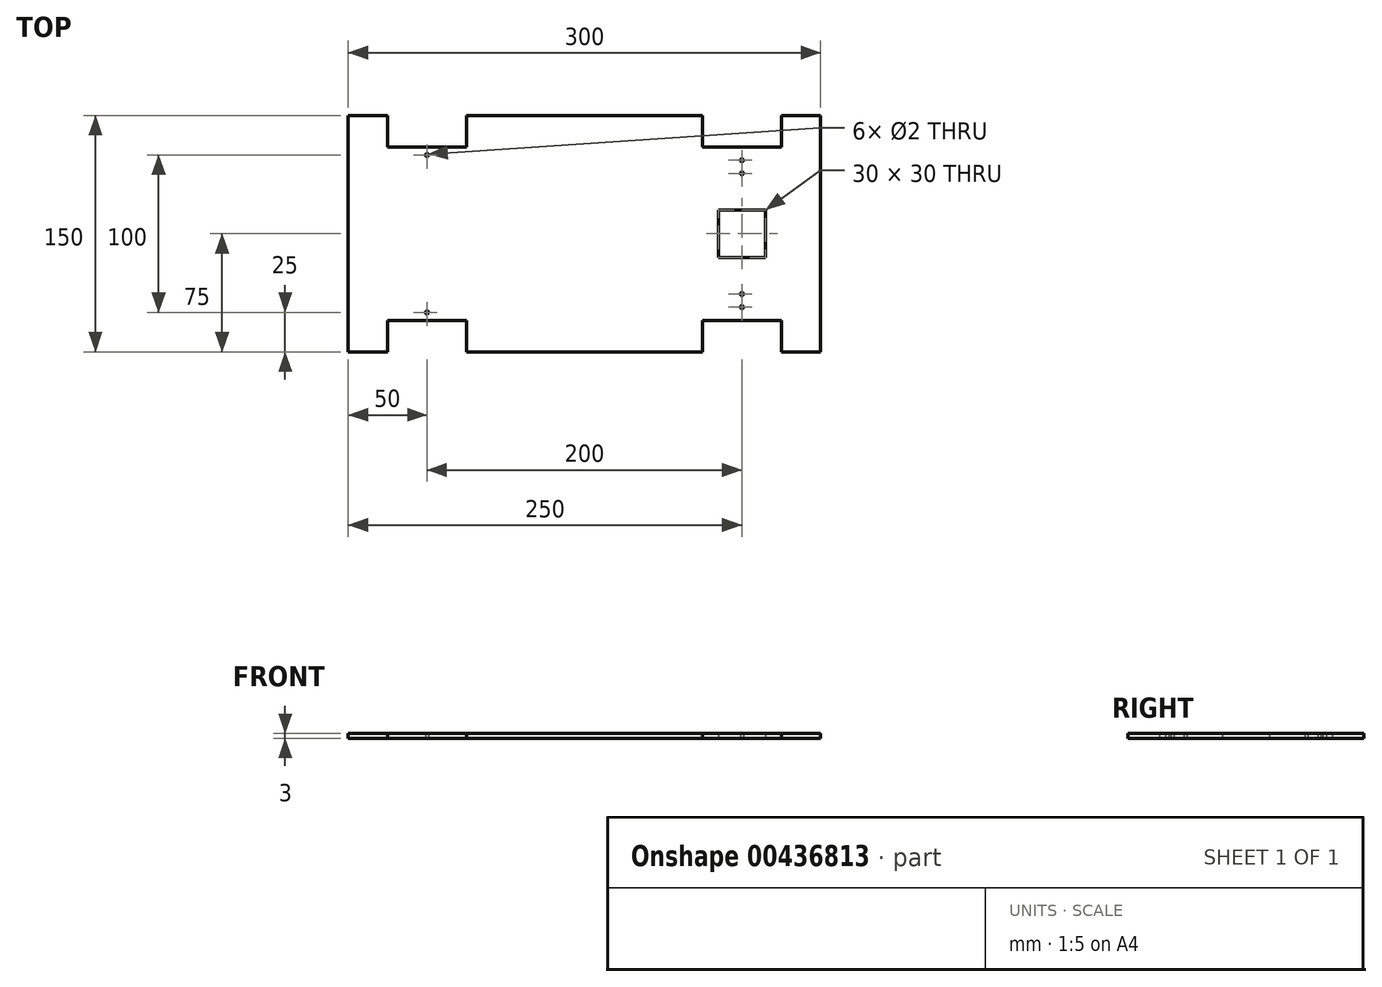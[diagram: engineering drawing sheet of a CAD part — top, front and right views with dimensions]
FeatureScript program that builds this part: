
annotation { "Feature Type Name" : "Feature", "Feature Type Description" : "" }
export const myFeature = defineFeature(function(context is Context, id is Id, definition is map)
    precondition{}
    {
        {
            var Q0;
            Q0=qCreatedBy(makeId("Top.planeOp"),FACE);
            var sketch = newSketch(context, id + "F0", { "sketchPlane" : qUnion([Q0])});
            skLineSegment(sketch, "E0.bottom", {"start": v(-150, 75) * mm, "end": v(-125, 75) * mm});
            skLineSegment(sketch, "E0.top", {"start": v(-150, -75) * mm, "end": v(-125, -75) * mm});
            skLineSegment(sketch, "E0.left", {"start": v(-150, 75) * mm, "end": v(-150, -75) * mm});
            skLineSegment(sketch, "E0.right", {"start": v(150, 75) * mm, "end": v(150, -75) * mm});
            skPoint(sketch, "E0.middle", {"position": v(0, 0) * mm});
            skCircle(sketch, "E1", {"center": v(-100, 50) * mm, "radius": 1 * mm});
            skCircle(sketch, "E2", {"center": v(-100, -50) * mm, "radius": 1 * mm});
            skCircle(sketch, "E3.MirrorC", {"center": v(100, -46.67) * mm, "radius": 1 * mm});
            skCircle(sketch, "E4.MirrorC", {"center": v(100, 46.67) * mm, "radius": 1 * mm});
            skLineSegment(sketch, "E5.left", {"start": v(-125, 75) * mm, "end": v(-125, 55) * mm});
            skLineSegment(sketch, "E6.MirrorCS", {"start": v(-75, 75) * mm, "end": v(-75, 55) * mm});
            skLineSegment(sketch, "E7", {"start": v(-125, 55) * mm, "end": v(-75, 55) * mm});
            skLineSegment(sketch, "E8.MirrorCS", {"start": v(125, 55) * mm, "end": v(75, 55) * mm});
            skLineSegment(sketch, "E9.MirrorCS", {"start": v(125, -55) * mm, "end": v(75, -55) * mm});
            skLineSegment(sketch, "E10.MirrorCS", {"start": v(-125, -55) * mm, "end": v(-75, -55) * mm});
            skLineSegment(sketch, "E11.trimOffspring", {"start": v(-75, 75) * mm, "end": v(75, 75) * mm});
            skLineSegment(sketch, "E12.trimOffspring", {"start": v(125, 75) * mm, "end": v(150, 75) * mm});
            skLineSegment(sketch, "E13.trimOffspring", {"start": v(-75, -75) * mm, "end": v(75, -75) * mm});
            skCircle(sketch, "E14", {"center": v(100, 38.33) * mm, "radius": 1 * mm});
            skCircle(sketch, "E15", {"center": v(100, -38.33) * mm, "radius": 1 * mm});
            skLineSegment(sketch, "E16.bottom", {"start": v(115, 15) * mm, "end": v(85, 15) * mm});
            skLineSegment(sketch, "E16.top", {"start": v(115, -15) * mm, "end": v(85, -15) * mm});
            skLineSegment(sketch, "E16.left", {"start": v(115, 15) * mm, "end": v(115, -15) * mm});
            skLineSegment(sketch, "E16.right", {"start": v(85, 15) * mm, "end": v(85, -15) * mm});
            skPoint(sketch, "E16.middle", {"position": v(100, 0) * mm});
            skPoint(sketch, "E17.endSnap0", {"position": v(-100, 0) * mm});
            skLineSegment(sketch, "E18.MirrorCS", {"start": v(-75, -75) * mm, "end": v(-75, -55) * mm});
            skLineSegment(sketch, "E19.MirrorCS", {"start": v(-125, -75) * mm, "end": v(-125, -55) * mm});
            skLineSegment(sketch, "E20.MirrorCS", {"start": v(125, -75) * mm, "end": v(125, -55) * mm});
            skLineSegment(sketch, "E21.MirrorCS", {"start": v(75, -75) * mm, "end": v(75, -55) * mm});
            skLineSegment(sketch, "E22.MirrorCS", {"start": v(75, 75) * mm, "end": v(75, 55) * mm});
            skLineSegment(sketch, "E23.MirrorCS", {"start": v(125, 75) * mm, "end": v(125, 55) * mm});
            skLineSegment(sketch, "E24", {"start": v(125, -75) * mm, "end": v(150, -75) * mm});
            skSolve(sketch);
        }
        {
            var Q0;
            Q0=makeQuery(id+"F0.imprint","IMPRINT",FACE,{"disambiguationData":[TD([[makeQuery(id+"F0.imprint","IMPRINT",EDGE,{"derivedFrom":sQuery(id+"F0.wireOp",EDGE,"E0.bottom")}),-1.0]])]});
            extrude(context, id + "F1", {"entities" : qUnion([Q0]), "depth" : 3 * mm});
        }
    });
